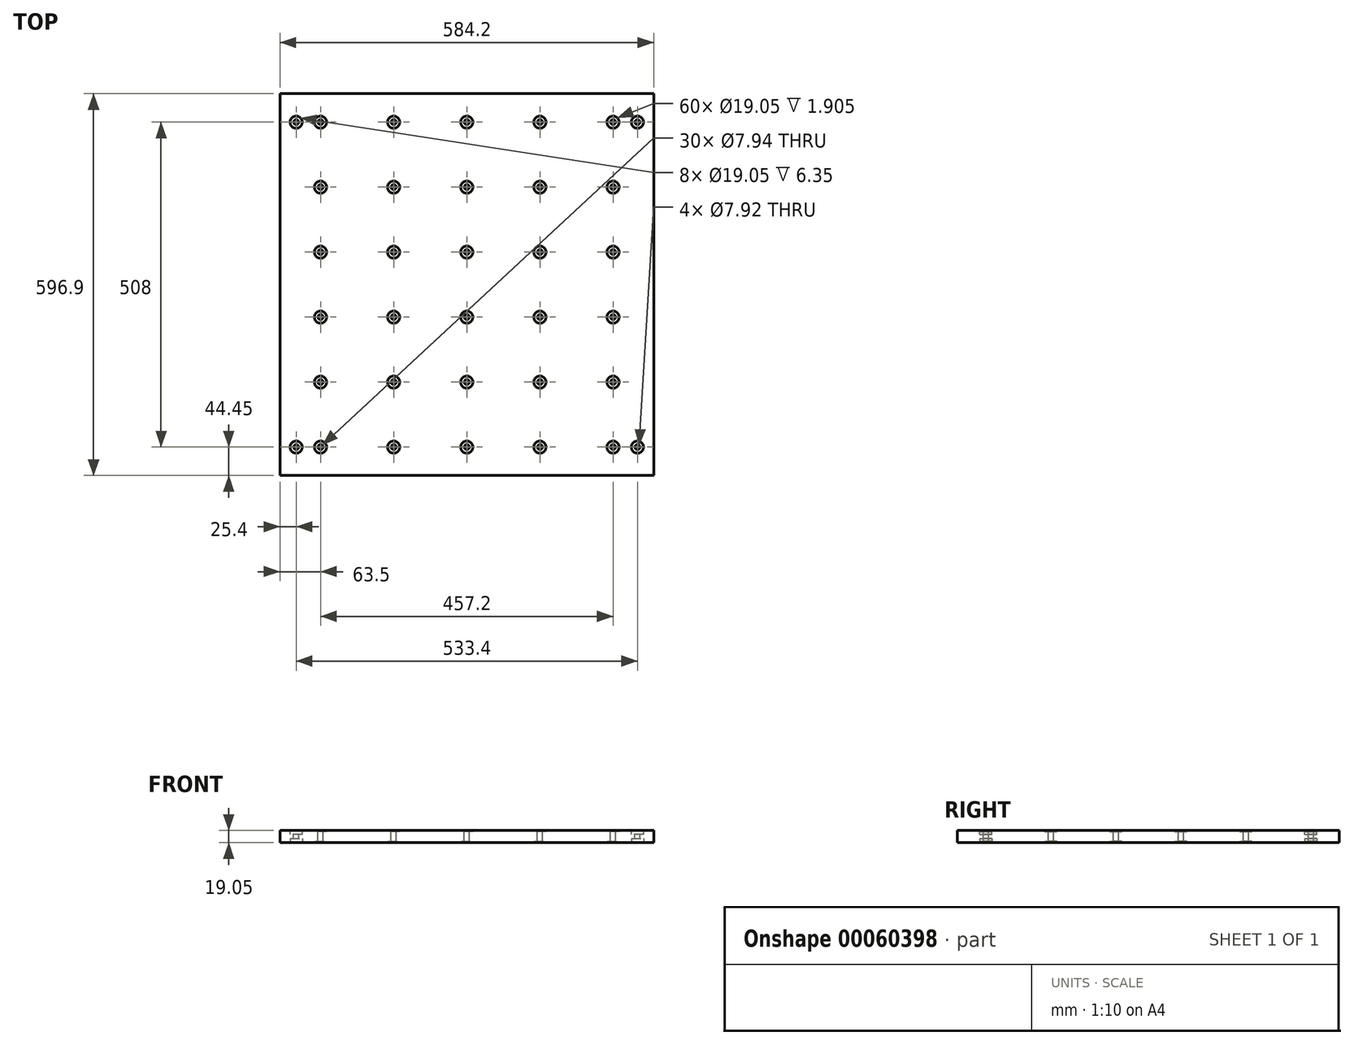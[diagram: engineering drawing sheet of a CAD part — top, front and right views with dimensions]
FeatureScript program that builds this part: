
annotation { "Feature Type Name" : "Feature", "Feature Type Description" : "" }
export const myFeature = defineFeature(function(context is Context, id is Id, definition is map)
    precondition{}
    {
        {
            var Q0;
            Q0=qCreatedBy(makeId("Top.planeOp"),FACE);
            var sketch = newSketch(context, id + "F0", { "sketchPlane" : qUnion([Q0])});
            skLineSegment(sketch, "E0.bottom", {"start": v(0, 0) * mm, "end": v(584.2, 0) * mm});
            skLineSegment(sketch, "E0.top", {"start": v(0, -596.9) * mm, "end": v(584.2, -596.9) * mm});
            skLineSegment(sketch, "E0.left", {"start": v(0, 0) * mm, "end": v(0, -596.9) * mm});
            skLineSegment(sketch, "E0.right", {"start": v(584.2, 0) * mm, "end": v(584.2, -596.9) * mm});
            skSolve(sketch);
        }
        {
            var Q0;
            Q0 = qSketchRegion(id + "F0", true);
            extrude(context, id + "F1", {"entities" : qUnion([Q0]), "depth" : 19.05 * mm});
        }
        {
            var Q0;
            Q0=makeQuery(id+"F1.opExtrude","CAP_FACE",FACE,{"disambiguationData":[OSD([sQuery(id+"F0.wireOp",EDGE,"E0.bottom"),sQuery(id+"F0.wireOp",EDGE,"E0.top"),sQuery(id+"F0.wireOp",EDGE,"E0.left"),sQuery(id+"F0.wireOp",EDGE,"E0.right")])],"isStart":false});
            var sketch = newSketch(context, id + "F2", { "sketchPlane" : qUnion([Q0])});
            skCircle(sketch, "E1", {"center": v(25.4, -552.45) * mm, "radius": 9.53 * mm});
            skCircle(sketch, "E2.0.1.0", {"center": v(25.4, -44.45) * mm, "radius": 9.53 * mm});
            skCircle(sketch, "E2.1.0.0", {"center": v(558.8, -552.45) * mm, "radius": 9.53 * mm});
            skCircle(sketch, "E2.1.1.0", {"center": v(558.8, -44.45) * mm, "radius": 9.53 * mm});
            skLineSegment(sketch, "E2.direction1", {"start": v(25.4, -552.45) * mm, "end": v(558.8, -552.45) * mm, "construction": true});
            skLineSegment(sketch, "E2.direction2", {"start": v(25.4, -552.45) * mm, "end": v(25.4, -44.45) * mm, "construction": true});
            skSolve(sketch);
        }
        {
            var Q0;
            Q0 = qSketchRegion(id + "F2", true);
            extrude(context, id + "F3", {"entities" : qUnion([Q0]), "operationType" : NewBodyOperationType.REMOVE, "oppositeDirection" : true, "depth" : 6.35 * mm});
        }
        {
            var Q0;
            Q0=makeQuery(id+"F1.opExtrude","CAP_FACE",FACE,{"disambiguationData":[OSD([sQuery(id+"F0.wireOp",EDGE,"E0.bottom"),sQuery(id+"F0.wireOp",EDGE,"E0.top"),sQuery(id+"F0.wireOp",EDGE,"E0.left"),sQuery(id+"F0.wireOp",EDGE,"E0.right")])],"isStart":false});
            var sketch = newSketch(context, id + "F4", { "sketchPlane" : qUnion([Q0])});
            skCircle(sketch, "E3", {"center": v(25.4, -552.45) * mm, "radius": 3.96 * mm});
            skCircle(sketch, "E4.0.1.0", {"center": v(25.4, -44.45) * mm, "radius": 3.96 * mm});
            skCircle(sketch, "E4.1.0.0", {"center": v(558.8, -552.45) * mm, "radius": 3.96 * mm});
            skCircle(sketch, "E4.1.1.0", {"center": v(558.8, -44.45) * mm, "radius": 3.96 * mm});
            skLineSegment(sketch, "E4.direction1", {"start": v(25.4, -552.45) * mm, "end": v(558.8, -552.45) * mm, "construction": true});
            skLineSegment(sketch, "E4.direction2", {"start": v(25.4, -552.45) * mm, "end": v(25.4, -44.45) * mm, "construction": true});
            skSolve(sketch);
        }
        {
            var Q0;
            Q0 = qSketchRegion(id + "F4", true);
            extrude(context, id + "F5", {"entities" : qUnion([Q0]), "operationType" : NewBodyOperationType.REMOVE, "endBound" : BoundingType.THROUGH_ALL, "oppositeDirection" : true, "depth" : 25.4 * mm});
        }
        {
            var Q0;
            Q0=makeQuery(id+"F1.opExtrude","CAP_FACE",FACE,{"disambiguationData":[OSD([sQuery(id+"F0.wireOp",EDGE,"E0.bottom"),sQuery(id+"F0.wireOp",EDGE,"E0.top"),sQuery(id+"F0.wireOp",EDGE,"E0.left"),sQuery(id+"F0.wireOp",EDGE,"E0.right")])],"isStart":true});
            var sketch = newSketch(context, id + "F6", { "sketchPlane" : qUnion([Q0])});
            skCircle(sketch, "E5", {"center": v(25.4, 44.45) * mm, "radius": 9.53 * mm});
            skCircle(sketch, "E6.0.1.0", {"center": v(25.4, 552.45) * mm, "radius": 9.53 * mm});
            skCircle(sketch, "E6.1.0.0", {"center": v(558.8, 44.45) * mm, "radius": 9.53 * mm});
            skCircle(sketch, "E6.1.1.0", {"center": v(558.8, 552.45) * mm, "radius": 9.53 * mm});
            skLineSegment(sketch, "E6.direction1", {"start": v(25.4, 44.45) * mm, "end": v(558.8, 44.45) * mm, "construction": true});
            skLineSegment(sketch, "E6.direction2", {"start": v(25.4, 44.45) * mm, "end": v(25.4, 552.45) * mm, "construction": true});
            skSolve(sketch);
        }
        {
            var Q0;
            Q0 = qSketchRegion(id + "F6", true);
            extrude(context, id + "F7", {"entities" : qUnion([Q0]), "operationType" : NewBodyOperationType.REMOVE, "oppositeDirection" : true, "depth" : 6.35 * mm});
        }
        {
            var Q0;
            Q0=makeQuery(id+"F1.opExtrude","CAP_FACE",FACE,{"disambiguationData":[OSD([sQuery(id+"F0.wireOp",EDGE,"E0.bottom"),sQuery(id+"F0.wireOp",EDGE,"E0.top"),sQuery(id+"F0.wireOp",EDGE,"E0.left"),sQuery(id+"F0.wireOp",EDGE,"E0.right")])],"isStart":false});
            var sketch = newSketch(context, id + "F8", { "sketchPlane" : qUnion([Q0])});
            skCircle(sketch, "E7", {"center": v(63.5, -552.45) * mm, "radius": 9.53 * mm});
            skCircle(sketch, "E8.0.1.0", {"center": v(63.5, -450.85) * mm, "radius": 9.53 * mm});
            skCircle(sketch, "E8.0.2.0", {"center": v(63.5, -349.25) * mm, "radius": 9.53 * mm});
            skCircle(sketch, "E8.0.3.0", {"center": v(63.5, -247.65) * mm, "radius": 9.53 * mm});
            skCircle(sketch, "E8.0.4.0", {"center": v(63.5, -146.05) * mm, "radius": 9.53 * mm});
            skCircle(sketch, "E8.0.5.0", {"center": v(63.5, -44.45) * mm, "radius": 9.53 * mm});
            skCircle(sketch, "E8.1.0.0", {"center": v(177.8, -552.45) * mm, "radius": 9.53 * mm});
            skCircle(sketch, "E8.1.1.0", {"center": v(177.8, -450.85) * mm, "radius": 9.53 * mm});
            skCircle(sketch, "E8.1.2.0", {"center": v(177.8, -349.25) * mm, "radius": 9.53 * mm});
            skCircle(sketch, "E8.1.3.0", {"center": v(177.8, -247.65) * mm, "radius": 9.53 * mm});
            skCircle(sketch, "E8.1.4.0", {"center": v(177.8, -146.05) * mm, "radius": 9.53 * mm});
            skCircle(sketch, "E8.1.5.0", {"center": v(177.8, -44.45) * mm, "radius": 9.53 * mm});
            skCircle(sketch, "E8.2.0.0", {"center": v(292.1, -552.45) * mm, "radius": 9.53 * mm});
            skCircle(sketch, "E8.2.1.0", {"center": v(292.1, -450.85) * mm, "radius": 9.53 * mm});
            skCircle(sketch, "E8.2.2.0", {"center": v(292.1, -349.25) * mm, "radius": 9.53 * mm});
            skCircle(sketch, "E8.2.3.0", {"center": v(292.1, -247.65) * mm, "radius": 9.53 * mm});
            skCircle(sketch, "E8.2.4.0", {"center": v(292.1, -146.05) * mm, "radius": 9.53 * mm});
            skCircle(sketch, "E8.2.5.0", {"center": v(292.1, -44.45) * mm, "radius": 9.53 * mm});
            skCircle(sketch, "E8.3.0.0", {"center": v(406.4, -552.45) * mm, "radius": 9.53 * mm});
            skCircle(sketch, "E8.3.1.0", {"center": v(406.4, -450.85) * mm, "radius": 9.53 * mm});
            skCircle(sketch, "E8.3.2.0", {"center": v(406.4, -349.25) * mm, "radius": 9.53 * mm});
            skCircle(sketch, "E8.3.3.0", {"center": v(406.4, -247.65) * mm, "radius": 9.53 * mm});
            skCircle(sketch, "E8.3.4.0", {"center": v(406.4, -146.05) * mm, "radius": 9.53 * mm});
            skCircle(sketch, "E8.3.5.0", {"center": v(406.4, -44.45) * mm, "radius": 9.53 * mm});
            skCircle(sketch, "E8.4.0.0", {"center": v(520.7, -552.45) * mm, "radius": 9.53 * mm});
            skCircle(sketch, "E8.4.1.0", {"center": v(520.7, -450.85) * mm, "radius": 9.53 * mm});
            skCircle(sketch, "E8.4.2.0", {"center": v(520.7, -349.25) * mm, "radius": 9.53 * mm});
            skCircle(sketch, "E8.4.3.0", {"center": v(520.7, -247.65) * mm, "radius": 9.53 * mm});
            skCircle(sketch, "E8.4.4.0", {"center": v(520.7, -146.05) * mm, "radius": 9.53 * mm});
            skCircle(sketch, "E8.4.5.0", {"center": v(520.7, -44.45) * mm, "radius": 9.53 * mm});
            skLineSegment(sketch, "E8.direction1", {"start": v(63.5, -552.45) * mm, "end": v(177.8, -552.45) * mm, "construction": true});
            skLineSegment(sketch, "E8.direction2", {"start": v(63.5, -552.45) * mm, "end": v(63.5, -450.85) * mm, "construction": true});
            skSolve(sketch);
        }
        {
            var Q0;
            Q0 = qSketchRegion(id + "F8", true);
            extrude(context, id + "F9", {"entities" : qUnion([Q0]), "operationType" : NewBodyOperationType.REMOVE, "oppositeDirection" : true, "depth" : 1.9 * mm});
        }
        {
            var Q0;
            Q0=makeQuery(id+"F1.opExtrude","CAP_FACE",FACE,{"disambiguationData":[OSD([sQuery(id+"F0.wireOp",EDGE,"E0.bottom"),sQuery(id+"F0.wireOp",EDGE,"E0.top"),sQuery(id+"F0.wireOp",EDGE,"E0.left"),sQuery(id+"F0.wireOp",EDGE,"E0.right")])],"isStart":false});
            var sketch = newSketch(context, id + "F10", { "sketchPlane" : qUnion([Q0])});
            skCircle(sketch, "E9", {"center": v(63.5, -552.45) * mm, "radius": 3.97 * mm});
            skCircle(sketch, "E10.0.1.0", {"center": v(63.5, -450.85) * mm, "radius": 3.97 * mm});
            skCircle(sketch, "E10.0.2.0", {"center": v(63.5, -349.25) * mm, "radius": 3.97 * mm});
            skCircle(sketch, "E10.0.3.0", {"center": v(63.5, -247.65) * mm, "radius": 3.97 * mm});
            skCircle(sketch, "E10.0.4.0", {"center": v(63.5, -146.05) * mm, "radius": 3.97 * mm});
            skCircle(sketch, "E10.0.5.0", {"center": v(63.5, -44.45) * mm, "radius": 3.97 * mm});
            skCircle(sketch, "E10.1.0.0", {"center": v(177.8, -552.45) * mm, "radius": 3.97 * mm});
            skCircle(sketch, "E10.1.1.0", {"center": v(177.8, -450.85) * mm, "radius": 3.97 * mm});
            skCircle(sketch, "E10.1.2.0", {"center": v(177.8, -349.25) * mm, "radius": 3.97 * mm});
            skCircle(sketch, "E10.1.3.0", {"center": v(177.8, -247.65) * mm, "radius": 3.97 * mm});
            skCircle(sketch, "E10.1.4.0", {"center": v(177.8, -146.05) * mm, "radius": 3.97 * mm});
            skCircle(sketch, "E10.1.5.0", {"center": v(177.8, -44.45) * mm, "radius": 3.97 * mm});
            skCircle(sketch, "E10.2.0.0", {"center": v(292.1, -552.45) * mm, "radius": 3.97 * mm});
            skCircle(sketch, "E10.2.1.0", {"center": v(292.1, -450.85) * mm, "radius": 3.97 * mm});
            skCircle(sketch, "E10.2.2.0", {"center": v(292.1, -349.25) * mm, "radius": 3.97 * mm});
            skCircle(sketch, "E10.2.3.0", {"center": v(292.1, -247.65) * mm, "radius": 3.97 * mm});
            skCircle(sketch, "E10.2.4.0", {"center": v(292.1, -146.05) * mm, "radius": 3.97 * mm});
            skCircle(sketch, "E10.2.5.0", {"center": v(292.1, -44.45) * mm, "radius": 3.97 * mm});
            skCircle(sketch, "E10.3.0.0", {"center": v(406.4, -552.45) * mm, "radius": 3.97 * mm});
            skCircle(sketch, "E10.3.1.0", {"center": v(406.4, -450.85) * mm, "radius": 3.97 * mm});
            skCircle(sketch, "E10.3.2.0", {"center": v(406.4, -349.25) * mm, "radius": 3.97 * mm});
            skCircle(sketch, "E10.3.3.0", {"center": v(406.4, -247.65) * mm, "radius": 3.97 * mm});
            skCircle(sketch, "E10.3.4.0", {"center": v(406.4, -146.05) * mm, "radius": 3.97 * mm});
            skCircle(sketch, "E10.3.5.0", {"center": v(406.4, -44.45) * mm, "radius": 3.97 * mm});
            skCircle(sketch, "E10.4.0.0", {"center": v(520.7, -552.45) * mm, "radius": 3.97 * mm});
            skCircle(sketch, "E10.4.1.0", {"center": v(520.7, -450.85) * mm, "radius": 3.97 * mm});
            skCircle(sketch, "E10.4.2.0", {"center": v(520.7, -349.25) * mm, "radius": 3.97 * mm});
            skCircle(sketch, "E10.4.3.0", {"center": v(520.7, -247.65) * mm, "radius": 3.97 * mm});
            skCircle(sketch, "E10.4.4.0", {"center": v(520.7, -146.05) * mm, "radius": 3.97 * mm});
            skCircle(sketch, "E10.4.5.0", {"center": v(520.7, -44.45) * mm, "radius": 3.97 * mm});
            skLineSegment(sketch, "E10.direction1", {"start": v(63.5, -552.45) * mm, "end": v(177.8, -552.45) * mm, "construction": true});
            skLineSegment(sketch, "E10.direction2", {"start": v(63.5, -552.45) * mm, "end": v(63.5, -450.85) * mm, "construction": true});
            skSolve(sketch);
        }
        {
            var Q0;
            Q0 = qSketchRegion(id + "F10", true);
            extrude(context, id + "F11", {"entities" : qUnion([Q0]), "operationType" : NewBodyOperationType.REMOVE, "endBound" : BoundingType.THROUGH_ALL, "oppositeDirection" : true, "depth" : 25.4 * mm});
        }
        {
            var Q0;
            Q0=makeQuery(id+"F1.opExtrude","CAP_FACE",FACE,{"disambiguationData":[OSD([sQuery(id+"F0.wireOp",EDGE,"E0.bottom"),sQuery(id+"F0.wireOp",EDGE,"E0.top"),sQuery(id+"F0.wireOp",EDGE,"E0.left"),sQuery(id+"F0.wireOp",EDGE,"E0.right")])],"isStart":true});
            var sketch = newSketch(context, id + "F12", { "sketchPlane" : qUnion([Q0])});
            skCircle(sketch, "E11", {"center": v(63.5, 552.45) * mm, "radius": 9.53 * mm});
            skCircle(sketch, "E12.0.1.0", {"center": v(63.5, 450.85) * mm, "radius": 9.53 * mm});
            skCircle(sketch, "E12.0.2.0", {"center": v(63.5, 349.25) * mm, "radius": 9.53 * mm});
            skCircle(sketch, "E12.0.3.0", {"center": v(63.5, 247.65) * mm, "radius": 9.53 * mm});
            skCircle(sketch, "E12.0.4.0", {"center": v(63.5, 146.05) * mm, "radius": 9.53 * mm});
            skCircle(sketch, "E12.0.5.0", {"center": v(63.5, 44.45) * mm, "radius": 9.53 * mm});
            skCircle(sketch, "E12.1.0.0", {"center": v(177.8, 552.45) * mm, "radius": 9.53 * mm});
            skCircle(sketch, "E12.1.1.0", {"center": v(177.8, 450.85) * mm, "radius": 9.53 * mm});
            skCircle(sketch, "E12.1.2.0", {"center": v(177.8, 349.25) * mm, "radius": 9.53 * mm});
            skCircle(sketch, "E12.1.3.0", {"center": v(177.8, 247.65) * mm, "radius": 9.53 * mm});
            skCircle(sketch, "E12.1.4.0", {"center": v(177.8, 146.05) * mm, "radius": 9.53 * mm});
            skCircle(sketch, "E12.1.5.0", {"center": v(177.8, 44.45) * mm, "radius": 9.53 * mm});
            skCircle(sketch, "E12.2.0.0", {"center": v(292.1, 552.45) * mm, "radius": 9.53 * mm});
            skCircle(sketch, "E12.2.1.0", {"center": v(292.1, 450.85) * mm, "radius": 9.53 * mm});
            skCircle(sketch, "E12.2.2.0", {"center": v(292.1, 349.25) * mm, "radius": 9.53 * mm});
            skCircle(sketch, "E12.2.3.0", {"center": v(292.1, 247.65) * mm, "radius": 9.53 * mm});
            skCircle(sketch, "E12.2.4.0", {"center": v(292.1, 146.05) * mm, "radius": 9.53 * mm});
            skCircle(sketch, "E12.2.5.0", {"center": v(292.1, 44.45) * mm, "radius": 9.53 * mm});
            skCircle(sketch, "E12.3.0.0", {"center": v(406.4, 552.45) * mm, "radius": 9.53 * mm});
            skCircle(sketch, "E12.3.1.0", {"center": v(406.4, 450.85) * mm, "radius": 9.53 * mm});
            skCircle(sketch, "E12.3.2.0", {"center": v(406.4, 349.25) * mm, "radius": 9.53 * mm});
            skCircle(sketch, "E12.3.3.0", {"center": v(406.4, 247.65) * mm, "radius": 9.53 * mm});
            skCircle(sketch, "E12.3.4.0", {"center": v(406.4, 146.05) * mm, "radius": 9.53 * mm});
            skCircle(sketch, "E12.3.5.0", {"center": v(406.4, 44.45) * mm, "radius": 9.53 * mm});
            skCircle(sketch, "E12.4.0.0", {"center": v(520.7, 552.45) * mm, "radius": 9.53 * mm});
            skCircle(sketch, "E12.4.1.0", {"center": v(520.7, 450.85) * mm, "radius": 9.53 * mm});
            skCircle(sketch, "E12.4.2.0", {"center": v(520.7, 349.25) * mm, "radius": 9.53 * mm});
            skCircle(sketch, "E12.4.3.0", {"center": v(520.7, 247.65) * mm, "radius": 9.53 * mm});
            skCircle(sketch, "E12.4.4.0", {"center": v(520.7, 146.05) * mm, "radius": 9.53 * mm});
            skCircle(sketch, "E12.4.5.0", {"center": v(520.7, 44.45) * mm, "radius": 9.53 * mm});
            skLineSegment(sketch, "E12.direction1", {"start": v(63.5, 552.45) * mm, "end": v(177.8, 552.45) * mm, "construction": true});
            skLineSegment(sketch, "E12.direction2", {"start": v(63.5, 552.45) * mm, "end": v(63.5, 450.85) * mm, "construction": true});
            skSolve(sketch);
        }
        {
            var Q0;
            Q0 = qSketchRegion(id + "F12", true);
            extrude(context, id + "F13", {"entities" : qUnion([Q0]), "operationType" : NewBodyOperationType.REMOVE, "oppositeDirection" : true, "depth" : 1.9 * mm});
        }
    });
